# Revit family: 4408_Analog Heat Detector
name_source: partatom
category: Fire Alarm Devices
units: mm (PartAtom-declared; Revit-internal decimal feet)

## family parameters
Cut with Voids When Loaded = No
Host = Face
Maintain Annotation Orientation = No
OmniClass Number = 23.85.30.21
OmniClass Title = Environmental Detection/Registration
Part Type = Normal
Room Calculation Point = No
Round Connector Dimension = Use Diameter
Shared = No

## types (1)
- 4408_Analog Heat Detector
    Ambient Humidity = Maximum 95 % RH (Non condensing)
    Ambient Temperature Operating = A1: -20 / +25 / +50°C 
A2 S: -20 / +25 / +50°C
B S: -20 / +40 / +65 °C
    Ambient Temperature Storage = (-25 to +70 °C)
    Bases = Bases : 3312W
    CPR = 0786-CPR-21204
    Clearance Area = Clearance Area
    Current Active External LED = 4.3 mA
    Current Active Internal LED = 2.3 mA
    Current Quiescent = 0.3 mA
    Default Elevation = 1200 mm
    Description = Analog heat detector 4408 with 3312 analog base
    H_Base (mm) = 6 mm  [stored 0.019685 ft]
    H_Detector (mm) = 36 mm  [stored 0.11811 ft]
    H_Total (mm) = 42 mm  [stored 0.137795 ft]
    Ingress Protection Rating = IP51
    Manufacturer = Panasonic
    Max_Wire Size = Ø 1.6 mm (2 mm²)
    Min_Wire Size = Ø 0.6 mm (0.3 mm²)
    Model = 4408
    Omniclass Code = 23.85.30.21.11.11.11
    Omniclass Description = Smoke Detectors
    Product Material = FR ABS and polycarbonate_Panasonic_White
    Short Circuit Isolator = No
    Tested and Approved = EN54-7
    Type Comments = The analog heat detector 4408 measures the temperature through a thermistor. The temperature range is 0°C to 100°C in steps of 0.5<unrecoverable-encoding: 3 bytes ef82b0>C. Algorithms for category A1, A2 S, and B S are used for detectors in NORMAL mode. The algorithm is programmed via EBLWin.
    URL = https://www.panasonic-fire-security.com
    Uniclass 2015 Code = Pr_75_80_30_27
    Uniclass 2015 Description = Fire and smoke detector bases
    Uniformat 2010  Code = D7050
    Uniformat 2010 Description = Detection and Alarm
    Vds Approval = G208109
    Version = RVT20
    Voltage Allowed = 12 – 30 V DC
    Voltage Normal = 24V DC
    Weight = 51g
    ø (mm) = 102 mm

note: [stored X ft] marks values corroborated as IEEE doubles in the binary element streams (Revit-internal decimal feet)

## geometry (parser evidence)
native form markers: Blend x82, Sweep x12
no freeform markers — native parametric forms only
